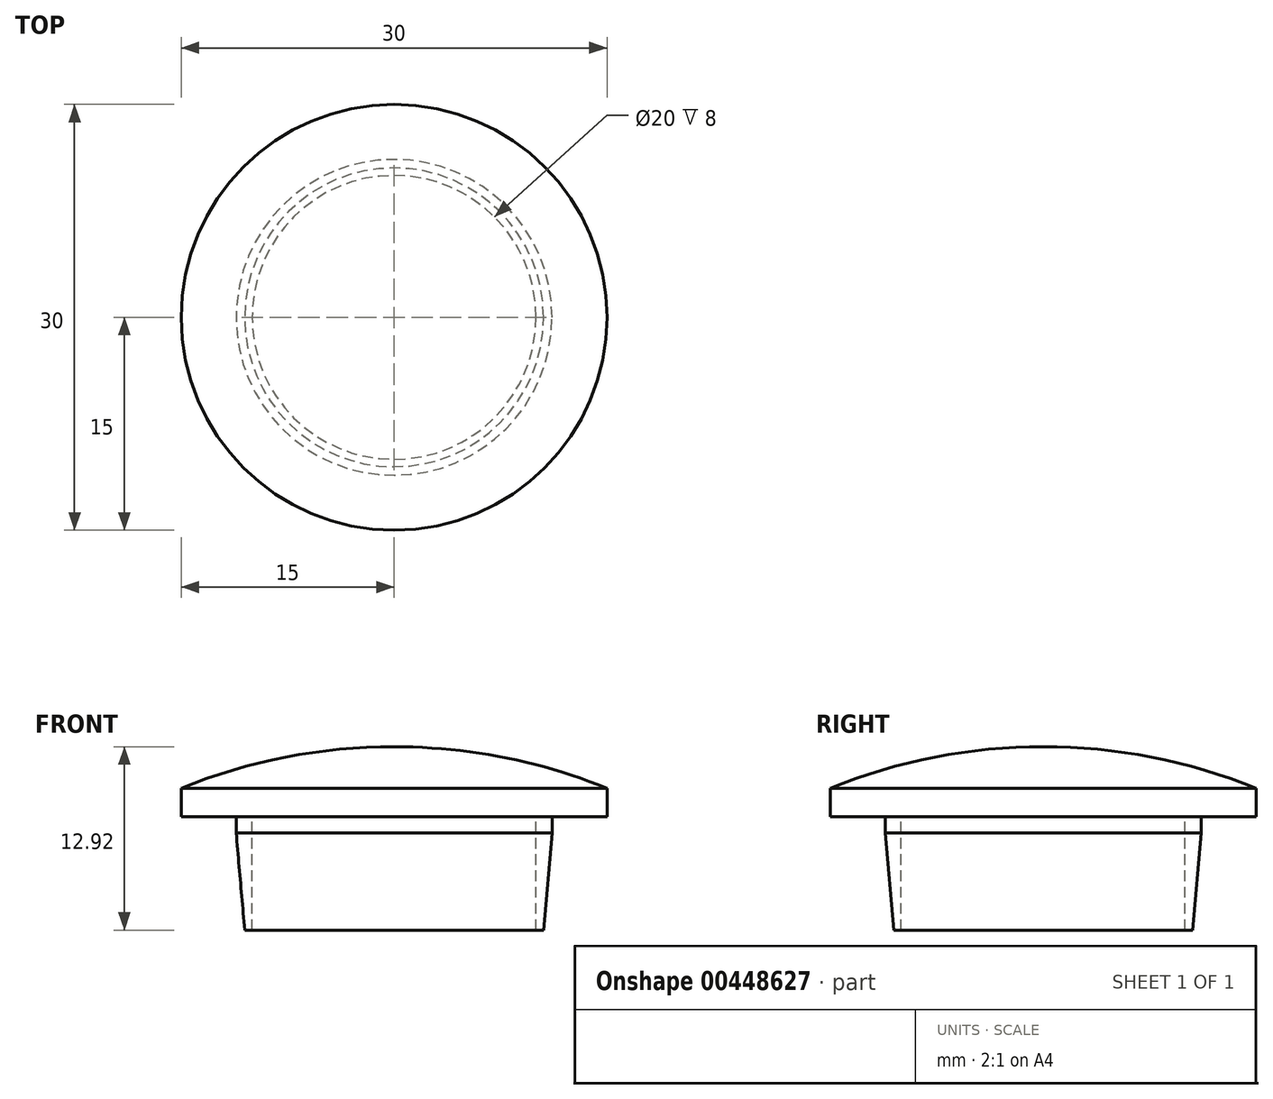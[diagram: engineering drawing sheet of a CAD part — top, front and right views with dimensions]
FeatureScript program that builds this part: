
annotation { "Feature Type Name" : "Feature", "Feature Type Description" : "" }
export const myFeature = defineFeature(function(context is Context, id is Id, definition is map)
    precondition{}
    {
        {
            var Q0;
            Q0=qCreatedBy(makeId("Top.planeOp"),FACE);
            var sketch = newSketch(context, id + "F0", { "sketchPlane" : qUnion([Q0])});
            skCircle(sketch, "E0", {"center": v(0, 0) * mm, "radius": 15 * mm});
            skSolve(sketch);
        }
        {
            var Q0;
            Q0 = qSketchRegion(id + "F0", true);
            extrude(context, id + "F1", {"entities" : qUnion([Q0]), "depth" : 2 * mm});
        }
        {
            var Q0;
            Q0=makeQuery(id+"F1.opExtrude","CAP_FACE",FACE,{"disambiguationData":[OSD([sQuery(id+"F0.wireOp",EDGE,"E0")])],"isStart":true});
            var sketch = newSketch(context, id + "F2", { "sketchPlane" : qUnion([Q0])});
            skCircle(sketch, "E1", {"center": v(0, 0) * mm, "radius": 11.12 * mm});
            skCircle(sketch, "E2", {"center": v(0, 0) * mm, "radius": 10 * mm});
            skSolve(sketch);
        }
        {
            var Q0;
            Q0 = qSketchRegion(id + "F2", true);
            extrude(context, id + "F3", {"entities" : qUnion([Q0]), "operationType" : NewBodyOperationType.ADD, "depth" : 8 * mm});
        }
        {
            var Q0;
            Q0=makeQuery(id+"F3.opExtrude","CAP_EDGE",EDGE,{"disambiguationData":[OSD([sQuery(id+"F2.wireOp",EDGE,"E1")])],"isStart":false});
            chamfer(context, id + "F4", {"entities" : qUnion([Q0]), "chamferType" : ChamferType.OFFSET_ANGLE, "width" : .6 * mm, "oppositeDirection" : false, "angle" : 85 * degree, "tangentPropagation" : true});
        }
        {
            var Q0;
            Q0=qCreatedBy(makeId("Front.planeOp"),FACE);
            var sketch = newSketch(context, id + "F5", { "sketchPlane" : qUnion([Q0])});
            skLineSegment(sketch, "E3.0", {"start": v(-15, 2) * mm, "end": v(15, 2) * mm});
            skArc(sketch, "E4", {"start": v(15, 2) * mm, "mid": v(0, 4.92) * mm, "end": v(-15, 2) * mm});
            skLineSegment(sketch, "E5", {"start": v(0, 2) * mm, "end": v(0, 4.92) * mm});
            skSolve(sketch);
        }
        {
            var Q0;
            {var subQ3=sQuery(id+"F5.wireOp",EDGE,"E5");Q0=makeQuery(id+"F5.imprint","IMPRINT",FACE,{"disambiguationData":[TD([[makeQuery(id+"F5.imprint","IMPRINT",EDGE,{"derivedFrom":subQ3}),-1.0]])]});}
            var Q1;
            Q1=sQuery(id+"F5.wireOp",EDGE,"E5");
            revolve(context, id + "F6", {"operationType" : NewBodyOperationType.ADD, "entities" : qUnion([Q0]), "axis" : qUnion([Q1]), "revolveType" : RevolveType.FULL});
        }
    });
